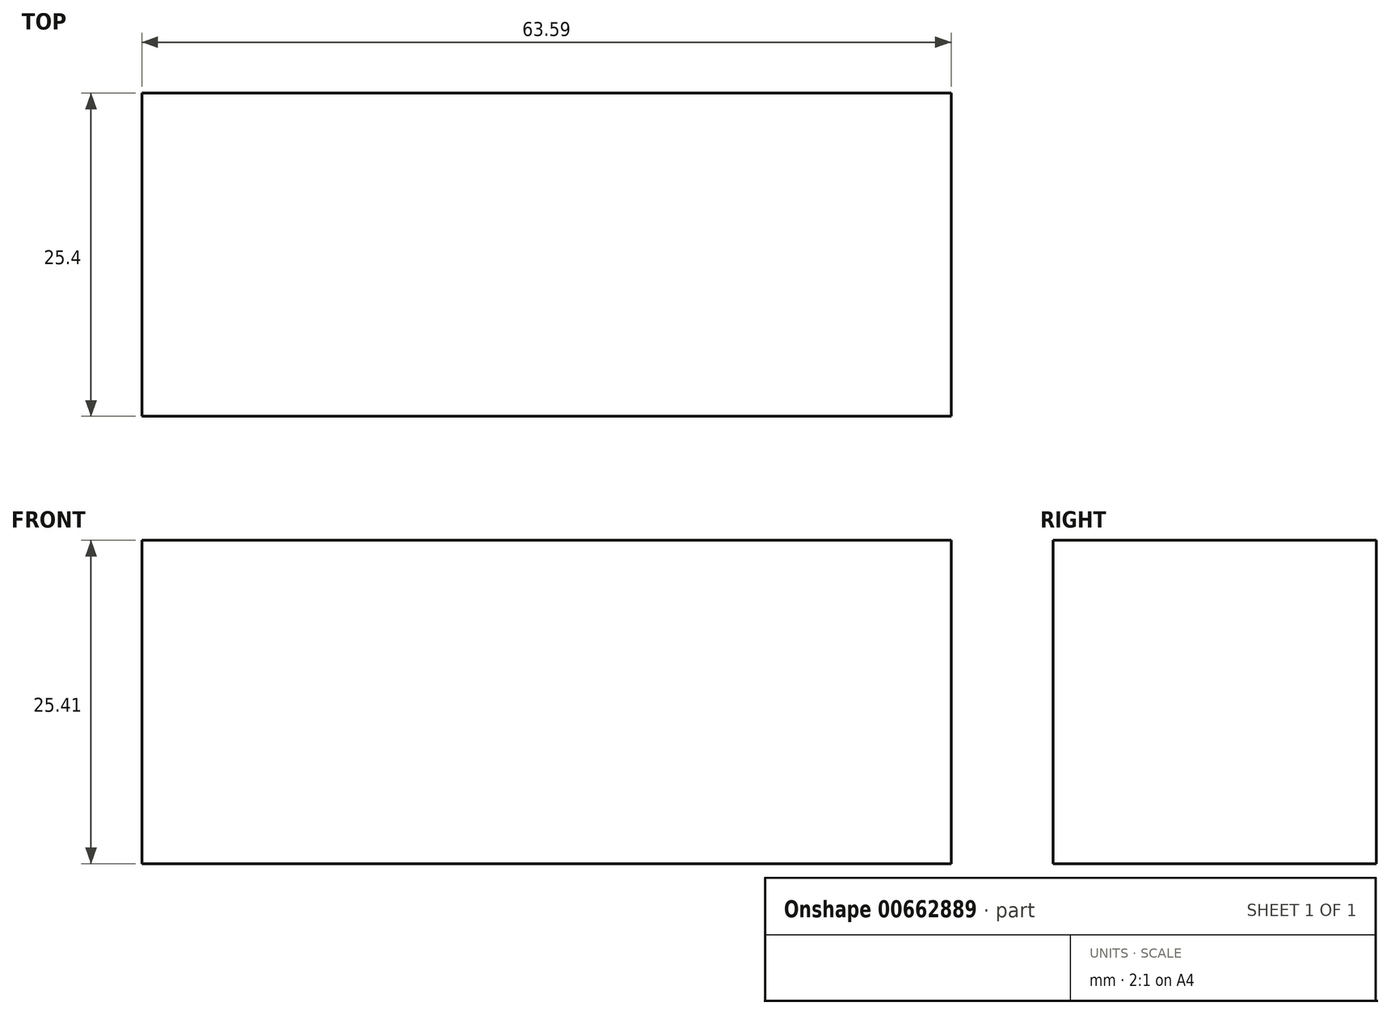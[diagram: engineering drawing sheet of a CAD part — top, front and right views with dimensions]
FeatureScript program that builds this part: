
annotation { "Feature Type Name" : "Feature", "Feature Type Description" : "" }
export const myFeature = defineFeature(function(context is Context, id is Id, definition is map)
    precondition{}
    {
        {
            var Q0;
            Q0=qCreatedBy(makeId("Front.planeOp"),FACE);
            var sketch = newSketch(context, id + "F0", { "sketchPlane" : qUnion([Q0])});
            skLineSegment(sketch, "E0.bottom", {"start": v(-8.38, 33.54) * mm, "end": v(53.5, 33.54) * mm});
            skLineSegment(sketch, "E0.top", {"start": v(-8.38, 8.25) * mm, "end": v(53.5, 8.25) * mm});
            skLineSegment(sketch, "E0.left", {"start": v(-8.38, 33.54) * mm, "end": v(-8.38, 8.25) * mm});
            skLineSegment(sketch, "E0.right", {"start": v(53.5, 33.54) * mm, "end": v(53.5, 8.25) * mm});
            skLineSegment(sketch, "E1.bottom", {"start": v(-8.38, 20.9) * mm, "end": v(-71.97, 20.9) * mm});
            skLineSegment(sketch, "E1.top", {"start": v(-8.38, -4.5) * mm, "end": v(-71.97, -4.5) * mm});
            skLineSegment(sketch, "E1.left", {"start": v(-8.38, 20.9) * mm, "end": v(-8.38, -4.5) * mm});
            skLineSegment(sketch, "E1.right", {"start": v(-71.97, 20.9) * mm, "end": v(-71.97, -4.5) * mm});
            skLineSegment(sketch, "E2.bottom", {"start": v(-28.07, -4.5) * mm, "end": v(-53.04, -4.5) * mm});
            skLineSegment(sketch, "E2.top", {"start": v(-28.07, -41) * mm, "end": v(-53.04, -41) * mm});
            skLineSegment(sketch, "E2.left", {"start": v(-28.07, -4.5) * mm, "end": v(-28.07, -41) * mm});
            skLineSegment(sketch, "E2.right", {"start": v(-53.04, -4.5) * mm, "end": v(-53.04, -41) * mm});
            skLineSegment(sketch, "E3.bottom", {"start": v(5.91, 33.54) * mm, "end": v(38.38, 33.54) * mm});
            skLineSegment(sketch, "E3.top", {"start": v(5.91, 40.5) * mm, "end": v(38.38, 40.5) * mm});
            skLineSegment(sketch, "E3.left", {"start": v(5.91, 33.54) * mm, "end": v(5.91, 40.5) * mm});
            skLineSegment(sketch, "E3.right", {"start": v(38.38, 33.54) * mm, "end": v(38.38, 40.5) * mm});
            skSolve(sketch);
        }
        {
            var Q0;
            {var subQ2=sQuery(id+"F0.wireOp",EDGE,"E1.bottom");Q0=makeQuery(id+"F0.imprint","IMPRINT",FACE,{"disambiguationData":[TD([[makeQuery(id+"F0.imprint","IMPRINT",EDGE,{"derivedFrom":subQ2}),1.0]])]});}
            extrude(context, id + "F1", {"entities" : qUnion([Q0]), "depth" : 25.4 * mm, "offsetDistance" : 25.4 * mm});
        }
    });
